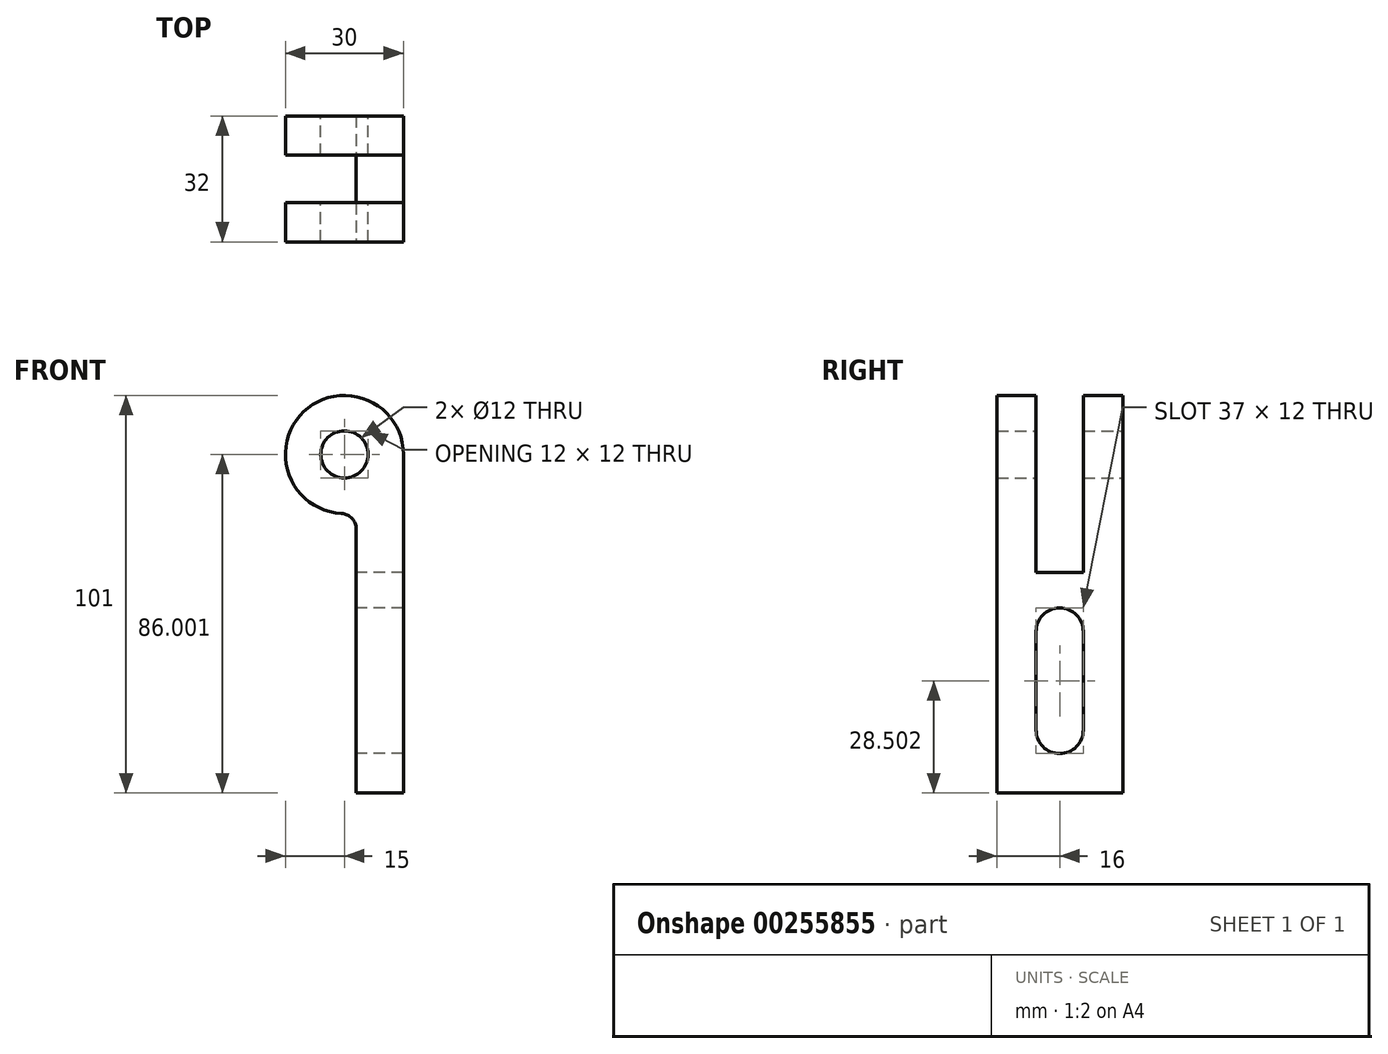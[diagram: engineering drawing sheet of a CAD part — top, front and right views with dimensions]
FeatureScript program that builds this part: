
annotation { "Feature Type Name" : "Feature", "Feature Type Description" : "" }
export const myFeature = defineFeature(function(context is Context, id is Id, definition is map)
    precondition{}
    {
        {
            var Q0;
            Q0=qCreatedBy(makeId("Front.planeOp"),FACE);
            var sketch = newSketch(context, id + "F0", { "sketchPlane" : qUnion([Q0])});
            skCircle(sketch, "E0", {"center": v(0, 58.16) * mm, "radius": 6 * mm});
            skArc(sketch, "E1", {"start": v(15, 58.16) * mm, "mid": v(-11.62, 67.65) * mm, "end": v(3, 43.46) * mm});
            skLineSegment(sketch, "E2.top", {"start": v(3, -27.84) * mm, "end": v(15, -27.84) * mm});
            skLineSegment(sketch, "E2.right", {"start": v(15, 58.16) * mm, "end": v(15, -27.84) * mm});
            skLineSegment(sketch, "E3.trimOffspring", {"start": v(3, 43.46) * mm, "end": v(3, -27.84) * mm});
            skSolve(sketch);
        }
        {
            var Q0;
            Q0=makeQuery(id+"F0.imprint","IMPRINT",FACE,{"disambiguationData":[TD([[makeQuery(id+"F0.imprint","IMPRINT",EDGE,{"derivedFrom":sQuery(id+"F0.wireOp",EDGE,"E0")}),-1.0]])]});
            extrude(context, id + "F1", {"entities" : qUnion([Q0]), "depth" : 32 * mm});
        }
        {
            var Q0;
            Q0=qCreatedBy(makeId("Right.planeOp"),FACE);
            cPlane(context, id + "F2", {"entities" : qUnion([Q0]), "cplaneType" : CPlaneType.OFFSET, "offset" : 40.8 * mm, "oppositeDirection" : true, "width" : 150 * mm, "height" : 150 * mm});
        }
        {
            var Q0;
            Q0=qCreatedBy(id+"F2.planeOp",FACE);
            var sketch = newSketch(context, id + "F3", { "sketchPlane" : qUnion([Q0])});
            skLineSegment(sketch, "E4.bottom", {"start": v(-10, 73.16) * mm, "end": v(-22, 73.16) * mm});
            skLineSegment(sketch, "E4.top", {"start": v(-10, 28.16) * mm, "end": v(-22, 28.16) * mm});
            skLineSegment(sketch, "E4.left", {"start": v(-10, 73.16) * mm, "end": v(-10, 28.16) * mm});
            skLineSegment(sketch, "E4.right", {"start": v(-22, 73.16) * mm, "end": v(-22, 28.16) * mm});
            skLineSegment(sketch, "E5", {"start": v(-32, 73.16) * mm, "end": v(0, 73.16) * mm});
            skArc(sketch, "E6", {"start": v(-10, 13.16) * mm, "mid": v(-16, 19.16) * mm, "end": v(-22, 13.16) * mm});
            skPoint(sketch, "E6.centerSnap0", {"position": v(-16, 28.16) * mm});
            skArc(sketch, "E7", {"start": v(-22, -11.84) * mm, "mid": v(-16, -17.84) * mm, "end": v(-10, -11.84) * mm});
            skLineSegment(sketch, "E8", {"start": v(-22, -11.84) * mm, "end": v(-22, 13.16) * mm});
            skLineSegment(sketch, "E9", {"start": v(-10, 13.16) * mm, "end": v(-10, -11.84) * mm});
            skArc(sketch, "E10", {"start": v(0, -11.84) * mm, "mid": v(-16, -27.84) * mm, "end": v(-32, -11.84) * mm});
            skLineSegment(sketch, "E11.0", {"start": v(0, 52.16) * mm, "end": v(0, 64.16) * mm});
            skPoint(sketch, "E12", {"position": v(0, 58.16) * mm});
            skLineSegment(sketch, "E13.0", {"start": v(0, 43.46) * mm, "end": v(0, -27.84) * mm});
            skLineSegment(sketch, "E14.0", {"start": v(-32, -27.84) * mm, "end": v(0, -27.84) * mm});
            skLineSegment(sketch, "E15.0", {"start": v(-32, 43.46) * mm, "end": v(-32, -27.84) * mm});
            skSolve(sketch);
        }
        {
            var Q0;
            {var subQ0=sQuery(id+"F3.wireOp",EDGE,"E13.0");var subQ1=sQuery(id+"F3.wireOp",EDGE,"E10");var subQ2=makeQuery(id+"F3.imprint","INTERSECT",VERTEX,{"derivedFrom":[subQ1,subQ0]});Q0=makeQuery(id+"F3.imprint","IMPRINT",FACE,{"disambiguationData":[TD([[makeQuery(id+"F3.imprint","IMPRINT",EDGE,{"disambiguationData":[TD([[subQ2,-1.0]])],"derivedFrom":subQ1}),1.0]])]});}
            var Q1;
            {var subQ0=sQuery(id+"F3.wireOp",EDGE,"E15.0");var subQ1=sQuery(id+"F3.wireOp",EDGE,"E10");var subQ2=makeQuery(id+"F3.imprint","INTERSECT",VERTEX,{"derivedFrom":[subQ1,subQ0]});Q1=makeQuery(id+"F3.imprint","IMPRINT",FACE,{"disambiguationData":[TD([[makeQuery(id+"F3.imprint","IMPRINT",EDGE,{"disambiguationData":[TD([[subQ2,1.0]])],"derivedFrom":subQ1}),1.0]])]});}
            var Q2;
            Q2=makeQuery(id+"F3.imprint","IMPRINT",FACE,{"disambiguationData":[TD([[makeQuery(id+"F3.imprint","IMPRINT",EDGE,{"derivedFrom":sQuery(id+"F3.wireOp",EDGE,"E6")}),1.0]])]});
            var Q3;
            Q3=makeQuery(id+"F3.imprint","IMPRINT",FACE,{"disambiguationData":[TD([[makeQuery(id+"F3.imprint","IMPRINT",EDGE,{"derivedFrom":sQuery(id+"F3.wireOp",EDGE,"E4.top")}),-1.0]])]});
            extrude(context, id + "F4", {"entities" : qUnion([Q0, Q1, Q2, Q3]), "operationType" : NewBodyOperationType.REMOVE, "endBound" : BoundingType.THROUGH_ALL, "depth" : 25 * mm});
        }
        {
            var Q0;
            {var subQ0=sQuery(id+"F0.wireOp",EDGE,"E3.trimOffspring");var subQ1=sQuery(id+"F0.wireOp",EDGE,"E1");Q0=makeQuery(id+"F4.boolean.opBoolean","SPLIT",EDGE,{"disambiguationData":[TD([makeQuery(id+"F4.opExtrude","SWEPT_FACE",FACE,{"disambiguationData":[OSD([sQuery(id+"F3.wireOp",EDGE,"E4.left")])]})])],"derivedFrom":makeQuery(id+"F1.opExtrude","SWEPT_EDGE",EDGE,{"disambiguationData":[OSD([subQ1,subQ0])]})});}
            var Q1;
            {var subQ0=sQuery(id+"F0.wireOp",EDGE,"E3.trimOffspring");var subQ1=sQuery(id+"F0.wireOp",EDGE,"E1");Q1=makeQuery(id+"F4.boolean.opBoolean","SPLIT",EDGE,{"disambiguationData":[TD([makeQuery(id+"F4.opExtrude","SWEPT_FACE",FACE,{"disambiguationData":[OSD([sQuery(id+"F3.wireOp",EDGE,"E4.right")])]})])],"derivedFrom":makeQuery(id+"F1.opExtrude","SWEPT_EDGE",EDGE,{"disambiguationData":[OSD([subQ1,subQ0])]})});}
            fillet(context, id + "F5", {"entities" : qUnion([Q0, Q1]), "radius" : 4 * mm, "tangentPropagation" : true, "allowEdgeOverflow" : false});
        }
    });
